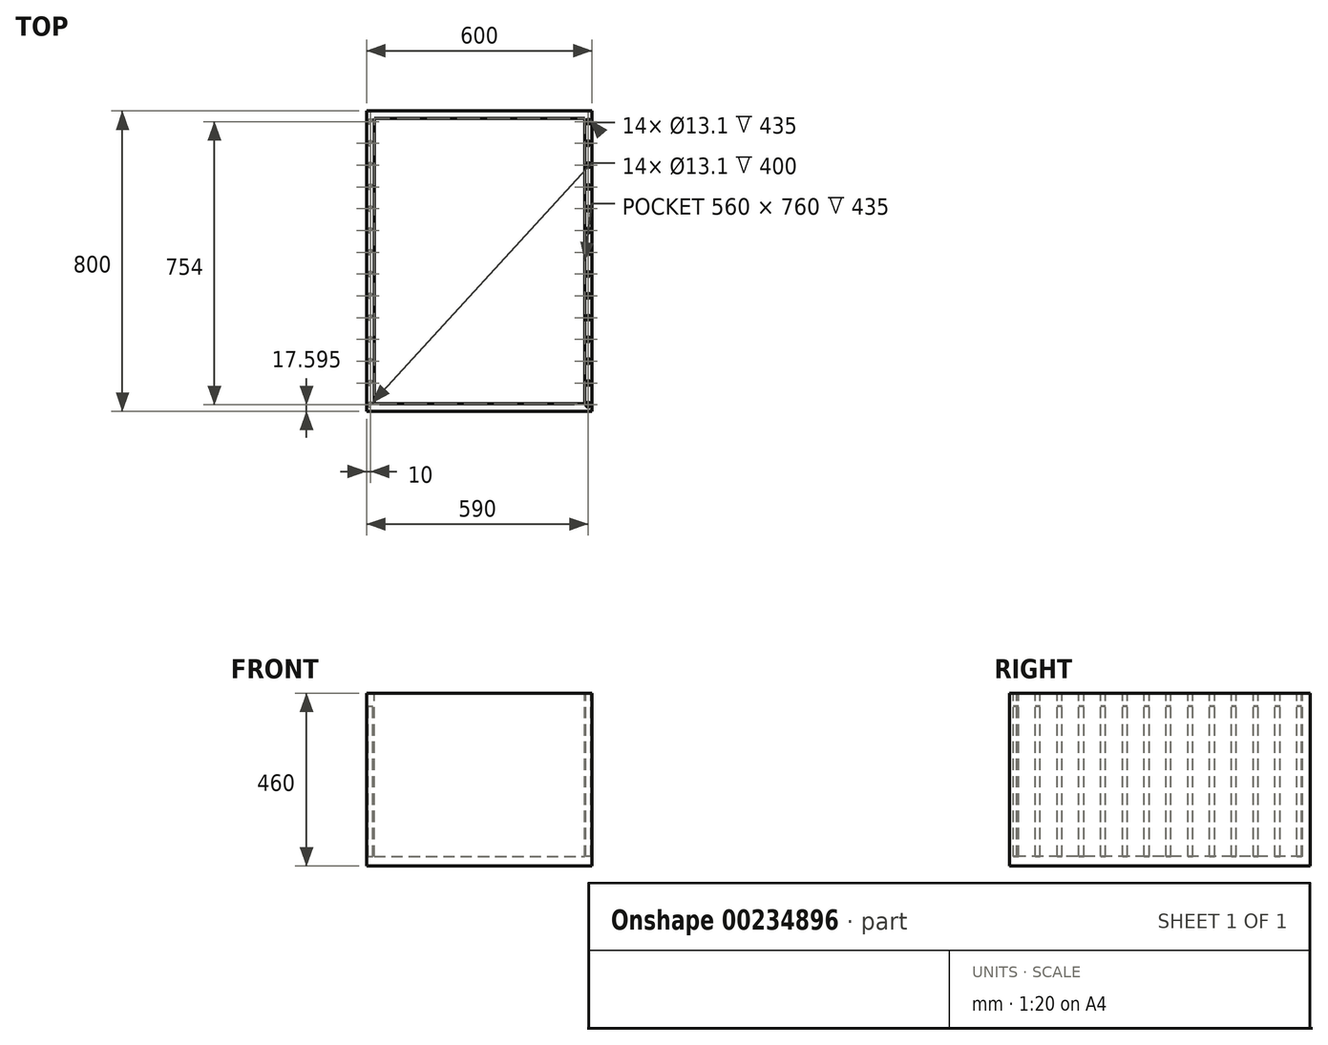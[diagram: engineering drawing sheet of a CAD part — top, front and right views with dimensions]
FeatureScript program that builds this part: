
annotation { "Feature Type Name" : "Feature", "Feature Type Description" : "" }
export const myFeature = defineFeature(function(context is Context, id is Id, definition is map)
    precondition{}
    {
        {
            var Q0;
            Q0=qCreatedBy(makeId("Top.planeOp"),FACE);
            var sketch = newSketch(context, id + "F0", { "sketchPlane" : qUnion([Q0])});
            skLineSegment(sketch, "E0.bottom", {"start": v(-307, 349) * mm, "end": v(293, 349) * mm});
            skLineSegment(sketch, "E0.top", {"start": v(-307, -451) * mm, "end": v(293, -451) * mm});
            skLineSegment(sketch, "E0.left", {"start": v(-307, 349) * mm, "end": v(-307, -451) * mm});
            skLineSegment(sketch, "E0.right", {"start": v(293, 349) * mm, "end": v(293, -451) * mm});
            skLineSegment(sketch, "E1.0", {"start": v(-287, 329) * mm, "end": v(273, 329) * mm});
            skLineSegment(sketch, "E1.1", {"start": v(-287, 329) * mm, "end": v(-287, -431) * mm});
            skLineSegment(sketch, "E1.2", {"start": v(-287, -431) * mm, "end": v(273, -431) * mm});
            skLineSegment(sketch, "E1.3", {"start": v(273, 329) * mm, "end": v(273, -431) * mm});
            skLineSegment(sketch, "E2", {"start": v(-307, -51) * mm, "end": v(-287, -51) * mm, "construction": true});
            skLineSegment(sketch, "E3", {"start": v(-287, -51) * mm, "end": v(-297, -51) * mm, "construction": true});
            skLineSegment(sketch, "E4", {"start": v(-297, -51) * mm, "end": v(-297, -27.4) * mm, "construction": true});
            skCircle(sketch, "E5", {"center": v(-297, -27.4) * mm, "radius": 6.55 * mm});
            skCircle(sketch, "E6.0.1.0", {"center": v(-297, 30.6) * mm, "radius": 6.55 * mm});
            skCircle(sketch, "E6.0.2.0", {"center": v(-297, 88.6) * mm, "radius": 6.55 * mm});
            skCircle(sketch, "E6.0.3.0", {"center": v(-297, 146.6) * mm, "radius": 6.55 * mm});
            skCircle(sketch, "E6.0.4.0", {"center": v(-297, 204.6) * mm, "radius": 6.55 * mm});
            skCircle(sketch, "E6.0.5.0", {"center": v(-297, 262.6) * mm, "radius": 6.55 * mm});
            skCircle(sketch, "E6.0.6.0", {"center": v(-297, 320.6) * mm, "radius": 6.55 * mm});
            skLineSegment(sketch, "E6.direction1", {"start": v(-297, -27.4) * mm, "end": v(-272, -27.4) * mm, "construction": true});
            skLineSegment(sketch, "E6.direction2", {"start": v(-297, -27.4) * mm, "end": v(-297, 30.6) * mm, "construction": true});
            skCircle(sketch, "E7.0.1.0", {"center": v(-297, -85.4) * mm, "radius": 6.55 * mm});
            skCircle(sketch, "E7.0.2.0", {"center": v(-297, -143.4) * mm, "radius": 6.55 * mm});
            skCircle(sketch, "E7.0.3.0", {"center": v(-297, -201.4) * mm, "radius": 6.55 * mm});
            skCircle(sketch, "E7.0.4.0", {"center": v(-297, -259.4) * mm, "radius": 6.55 * mm});
            skCircle(sketch, "E7.0.5.0", {"center": v(-297, -317.4) * mm, "radius": 6.55 * mm});
            skCircle(sketch, "E7.0.6.0", {"center": v(-297, -375.4) * mm, "radius": 6.55 * mm});
            skCircle(sketch, "E7.0.7.0", {"center": v(-297, -433.4) * mm, "radius": 6.55 * mm});
            skLineSegment(sketch, "E7.direction1", {"start": v(-297, -27.4) * mm, "end": v(-257, -27.4) * mm, "construction": true});
            skLineSegment(sketch, "E7.direction2", {"start": v(-297, -27.4) * mm, "end": v(-297, -85.4) * mm, "construction": true});
            skLineSegment(sketch, "E8", {"start": v(-7, 329) * mm, "end": v(-7, -431) * mm, "construction": true});
            skCircle(sketch, "E9.MirrorC", {"center": v(283, 320.6) * mm, "radius": 6.55 * mm});
            skCircle(sketch, "E10.MirrorC", {"center": v(283, 262.6) * mm, "radius": 6.55 * mm});
            skCircle(sketch, "E11.MirrorC", {"center": v(283, 204.6) * mm, "radius": 6.55 * mm});
            skCircle(sketch, "E12.MirrorC", {"center": v(283, 146.6) * mm, "radius": 6.55 * mm});
            skCircle(sketch, "E13.MirrorC", {"center": v(283, 88.6) * mm, "radius": 6.55 * mm});
            skCircle(sketch, "E14.MirrorC", {"center": v(283, 30.6) * mm, "radius": 6.55 * mm});
            skCircle(sketch, "E15.MirrorC", {"center": v(283, -27.4) * mm, "radius": 6.55 * mm});
            skCircle(sketch, "E16.MirrorC", {"center": v(283, -85.4) * mm, "radius": 6.55 * mm});
            skCircle(sketch, "E17.MirrorC", {"center": v(283, -143.4) * mm, "radius": 6.55 * mm});
            skCircle(sketch, "E18.MirrorC", {"center": v(283, -201.4) * mm, "radius": 6.55 * mm});
            skCircle(sketch, "E19.MirrorC", {"center": v(283, -259.4) * mm, "radius": 6.55 * mm});
            skCircle(sketch, "E20.MirrorC", {"center": v(283, -317.4) * mm, "radius": 6.55 * mm});
            skCircle(sketch, "E21.MirrorC", {"center": v(283, -375.4) * mm, "radius": 6.55 * mm});
            skCircle(sketch, "E22.MirrorC", {"center": v(283, -433.4) * mm, "radius": 6.55 * mm});
            skSolve(sketch);
        }
        {
            var Q0;
            Q0=makeQuery(id+"F0.imprint","IMPRINT",FACE,{"disambiguationData":[TD([[makeQuery(id+"F0.imprint","IMPRINT",EDGE,{"derivedFrom":sQuery(id+"F0.wireOp",EDGE,"E0.bottom")}),-1.0]])]});
            var Q1;
            Q1=makeQuery(id+"F0.imprint","IMPRINT",FACE,{"disambiguationData":[TD([[makeQuery(id+"F0.imprint","IMPRINT",EDGE,{"derivedFrom":sQuery(id+"F0.wireOp",EDGE,"E22.MirrorC")}),-1.0]])]});
            var Q2;
            Q2=makeQuery(id+"F0.imprint","IMPRINT",FACE,{"disambiguationData":[TD([[makeQuery(id+"F0.imprint","IMPRINT",EDGE,{"derivedFrom":sQuery(id+"F0.wireOp",EDGE,"E21.MirrorC")}),-1.0]])]});
            var Q3;
            Q3=makeQuery(id+"F0.imprint","IMPRINT",FACE,{"disambiguationData":[TD([[makeQuery(id+"F0.imprint","IMPRINT",EDGE,{"derivedFrom":sQuery(id+"F0.wireOp",EDGE,"E20.MirrorC")}),-1.0]])]});
            var Q4;
            Q4=makeQuery(id+"F0.imprint","IMPRINT",FACE,{"disambiguationData":[TD([[makeQuery(id+"F0.imprint","IMPRINT",EDGE,{"derivedFrom":sQuery(id+"F0.wireOp",EDGE,"E19.MirrorC")}),-1.0]])]});
            var Q5;
            Q5=makeQuery(id+"F0.imprint","IMPRINT",FACE,{"disambiguationData":[TD([[makeQuery(id+"F0.imprint","IMPRINT",EDGE,{"derivedFrom":sQuery(id+"F0.wireOp",EDGE,"E18.MirrorC")}),-1.0]])]});
            var Q6;
            Q6=makeQuery(id+"F0.imprint","IMPRINT",FACE,{"disambiguationData":[TD([[makeQuery(id+"F0.imprint","IMPRINT",EDGE,{"derivedFrom":sQuery(id+"F0.wireOp",EDGE,"E17.MirrorC")}),-1.0]])]});
            var Q7;
            Q7=makeQuery(id+"F0.imprint","IMPRINT",FACE,{"disambiguationData":[TD([[makeQuery(id+"F0.imprint","IMPRINT",EDGE,{"derivedFrom":sQuery(id+"F0.wireOp",EDGE,"E16.MirrorC")}),-1.0]])]});
            var Q8;
            Q8=makeQuery(id+"F0.imprint","IMPRINT",FACE,{"disambiguationData":[TD([[makeQuery(id+"F0.imprint","IMPRINT",EDGE,{"derivedFrom":sQuery(id+"F0.wireOp",EDGE,"E15.MirrorC")}),-1.0]])]});
            var Q9;
            Q9=makeQuery(id+"F0.imprint","IMPRINT",FACE,{"disambiguationData":[TD([[makeQuery(id+"F0.imprint","IMPRINT",EDGE,{"derivedFrom":sQuery(id+"F0.wireOp",EDGE,"E14.MirrorC")}),-1.0]])]});
            var Q10;
            Q10=makeQuery(id+"F0.imprint","IMPRINT",FACE,{"disambiguationData":[TD([[makeQuery(id+"F0.imprint","IMPRINT",EDGE,{"derivedFrom":sQuery(id+"F0.wireOp",EDGE,"E13.MirrorC")}),-1.0]])]});
            var Q11;
            Q11=makeQuery(id+"F0.imprint","IMPRINT",FACE,{"disambiguationData":[TD([[makeQuery(id+"F0.imprint","IMPRINT",EDGE,{"derivedFrom":sQuery(id+"F0.wireOp",EDGE,"E12.MirrorC")}),-1.0]])]});
            var Q12;
            Q12=makeQuery(id+"F0.imprint","IMPRINT",FACE,{"disambiguationData":[TD([[makeQuery(id+"F0.imprint","IMPRINT",EDGE,{"derivedFrom":sQuery(id+"F0.wireOp",EDGE,"E11.MirrorC")}),-1.0]])]});
            var Q13;
            Q13=makeQuery(id+"F0.imprint","IMPRINT",FACE,{"disambiguationData":[TD([[makeQuery(id+"F0.imprint","IMPRINT",EDGE,{"derivedFrom":sQuery(id+"F0.wireOp",EDGE,"E10.MirrorC")}),-1.0]])]});
            var Q14;
            Q14=makeQuery(id+"F0.imprint","IMPRINT",FACE,{"disambiguationData":[TD([[makeQuery(id+"F0.imprint","IMPRINT",EDGE,{"derivedFrom":sQuery(id+"F0.wireOp",EDGE,"E9.MirrorC")}),-1.0]])]});
            var Q15;
            Q15=makeQuery(id+"F0.imprint","IMPRINT",FACE,{"disambiguationData":[TD([[makeQuery(id+"F0.imprint","IMPRINT",EDGE,{"derivedFrom":sQuery(id+"F0.wireOp",EDGE,"E6.0.6.0")}),1.0]])]});
            var Q16;
            Q16=makeQuery(id+"F0.imprint","IMPRINT",FACE,{"disambiguationData":[TD([[makeQuery(id+"F0.imprint","IMPRINT",EDGE,{"derivedFrom":sQuery(id+"F0.wireOp",EDGE,"E6.0.5.0")}),1.0]])]});
            var Q17;
            Q17=makeQuery(id+"F0.imprint","IMPRINT",FACE,{"disambiguationData":[TD([[makeQuery(id+"F0.imprint","IMPRINT",EDGE,{"derivedFrom":sQuery(id+"F0.wireOp",EDGE,"E6.0.4.0")}),1.0]])]});
            var Q18;
            Q18=makeQuery(id+"F0.imprint","IMPRINT",FACE,{"disambiguationData":[TD([[makeQuery(id+"F0.imprint","IMPRINT",EDGE,{"derivedFrom":sQuery(id+"F0.wireOp",EDGE,"E6.0.3.0")}),1.0]])]});
            var Q19;
            Q19=makeQuery(id+"F0.imprint","IMPRINT",FACE,{"disambiguationData":[TD([[makeQuery(id+"F0.imprint","IMPRINT",EDGE,{"derivedFrom":sQuery(id+"F0.wireOp",EDGE,"E6.0.2.0")}),1.0]])]});
            var Q20;
            Q20=makeQuery(id+"F0.imprint","IMPRINT",FACE,{"disambiguationData":[TD([[makeQuery(id+"F0.imprint","IMPRINT",EDGE,{"derivedFrom":sQuery(id+"F0.wireOp",EDGE,"E6.0.1.0")}),1.0]])]});
            var Q21;
            Q21=makeQuery(id+"F0.imprint","IMPRINT",FACE,{"disambiguationData":[TD([[makeQuery(id+"F0.imprint","IMPRINT",EDGE,{"derivedFrom":sQuery(id+"F0.wireOp",EDGE,"E5")}),1.0]])]});
            var Q22;
            Q22=makeQuery(id+"F0.imprint","IMPRINT",FACE,{"disambiguationData":[TD([[makeQuery(id+"F0.imprint","IMPRINT",EDGE,{"derivedFrom":sQuery(id+"F0.wireOp",EDGE,"E7.0.1.0")}),1.0]])]});
            var Q23;
            Q23=makeQuery(id+"F0.imprint","IMPRINT",FACE,{"disambiguationData":[TD([[makeQuery(id+"F0.imprint","IMPRINT",EDGE,{"derivedFrom":sQuery(id+"F0.wireOp",EDGE,"E7.0.2.0")}),1.0]])]});
            var Q24;
            Q24=makeQuery(id+"F0.imprint","IMPRINT",FACE,{"disambiguationData":[TD([[makeQuery(id+"F0.imprint","IMPRINT",EDGE,{"derivedFrom":sQuery(id+"F0.wireOp",EDGE,"E7.0.3.0")}),1.0]])]});
            var Q25;
            Q25=makeQuery(id+"F0.imprint","IMPRINT",FACE,{"disambiguationData":[TD([[makeQuery(id+"F0.imprint","IMPRINT",EDGE,{"derivedFrom":sQuery(id+"F0.wireOp",EDGE,"E7.0.4.0")}),1.0]])]});
            var Q26;
            Q26=makeQuery(id+"F0.imprint","IMPRINT",FACE,{"disambiguationData":[TD([[makeQuery(id+"F0.imprint","IMPRINT",EDGE,{"derivedFrom":sQuery(id+"F0.wireOp",EDGE,"E7.0.5.0")}),1.0]])]});
            var Q27;
            Q27=makeQuery(id+"F0.imprint","IMPRINT",FACE,{"disambiguationData":[TD([[makeQuery(id+"F0.imprint","IMPRINT",EDGE,{"derivedFrom":sQuery(id+"F0.wireOp",EDGE,"E7.0.6.0")}),1.0]])]});
            var Q28;
            Q28=makeQuery(id+"F0.imprint","IMPRINT",FACE,{"disambiguationData":[TD([[makeQuery(id+"F0.imprint","IMPRINT",EDGE,{"derivedFrom":sQuery(id+"F0.wireOp",EDGE,"E7.0.7.0")}),1.0]])]});
            extrude(context, id + "F1", {"entities" : qUnion([Q0, Q1, Q2, Q3, Q4, Q5, Q6, Q7, Q8, Q9, Q10, Q11, Q12, Q13, Q14, Q15, Q16, Q17, Q18, Q19, Q20, Q21, Q22, Q23, Q24, Q25, Q26, Q27, Q28]), "oppositeDirection" : true, "depth" : 35 * mm});
        }
        {
            var Q0;
            Q0=makeQuery(id+"F1.opExtrude","CAP_FACE",FACE,{"disambiguationData":[OSD([sQuery(id+"F0.wireOp",EDGE,"E0.bottom"),sQuery(id+"F0.wireOp",EDGE,"E0.top"),sQuery(id+"F0.wireOp",EDGE,"E0.left"),sQuery(id+"F0.wireOp",EDGE,"E0.right"),sQuery(id+"F0.wireOp",EDGE,"E1.0"),sQuery(id+"F0.wireOp",EDGE,"E1.1"),sQuery(id+"F0.wireOp",EDGE,"E1.2"),sQuery(id+"F0.wireOp",EDGE,"E1.3")])],"isStart":false});
            var sketch = newSketch(context, id + "F2", { "sketchPlane" : qUnion([Q0])});
            skCircle(sketch, "E23.0", {"center": v(283, 85.4) * mm, "radius": 6.55 * mm});
            skCircle(sketch, "E23.1", {"center": v(283, -320.6) * mm, "radius": 6.55 * mm});
            skCircle(sketch, "E23.2", {"center": v(283, -204.6) * mm, "radius": 6.55 * mm});
            skCircle(sketch, "E23.3", {"center": v(283, -262.6) * mm, "radius": 6.55 * mm});
            skCircle(sketch, "E23.4", {"center": v(283, 143.4) * mm, "radius": 6.55 * mm});
            skCircle(sketch, "E23.5", {"center": v(283, 259.4) * mm, "radius": 6.55 * mm});
            skCircle(sketch, "E23.6", {"center": v(283, -146.6) * mm, "radius": 6.55 * mm});
            skCircle(sketch, "E23.7", {"center": v(283, 317.4) * mm, "radius": 6.55 * mm});
            skCircle(sketch, "E23.8", {"center": v(283, 201.4) * mm, "radius": 6.55 * mm});
            skCircle(sketch, "E23.9", {"center": v(283, -30.6) * mm, "radius": 6.55 * mm});
            skCircle(sketch, "E23.10", {"center": v(283, 27.4) * mm, "radius": 6.55 * mm});
            skCircle(sketch, "E23.11", {"center": v(283, 433.4) * mm, "radius": 6.55 * mm});
            skCircle(sketch, "E23.12", {"center": v(283, 375.4) * mm, "radius": 6.55 * mm});
            skCircle(sketch, "E23.13", {"center": v(283, -88.6) * mm, "radius": 6.55 * mm});
            skCircle(sketch, "E24.0", {"center": v(-297, -30.6) * mm, "radius": 6.55 * mm});
            skCircle(sketch, "E24.1", {"center": v(-297, 259.4) * mm, "radius": 6.55 * mm});
            skCircle(sketch, "E24.2", {"center": v(-297, -320.6) * mm, "radius": 6.55 * mm});
            skLineSegment(sketch, "E24.3", {"start": v(-297, 51) * mm, "end": v(-297, 27.4) * mm});
            skCircle(sketch, "E24.4", {"center": v(-297, -204.6) * mm, "radius": 6.55 * mm});
            skCircle(sketch, "E24.5", {"center": v(-297, -146.6) * mm, "radius": 6.55 * mm});
            skCircle(sketch, "E24.6", {"center": v(-297, 201.4) * mm, "radius": 6.55 * mm});
            skCircle(sketch, "E24.7", {"center": v(-297, 317.4) * mm, "radius": 6.55 * mm});
            skCircle(sketch, "E24.8", {"center": v(-297, 375.4) * mm, "radius": 6.55 * mm});
            skCircle(sketch, "E24.9", {"center": v(-297, -88.6) * mm, "radius": 6.55 * mm});
            skCircle(sketch, "E24.10", {"center": v(-297, 143.4) * mm, "radius": 6.55 * mm});
            skCircle(sketch, "E24.11", {"center": v(-297, 27.4) * mm, "radius": 6.55 * mm});
            skLineSegment(sketch, "E24.12", {"start": v(-297, 27.4) * mm, "end": v(-297, 85.4) * mm});
            skCircle(sketch, "E24.13", {"center": v(-297, -262.6) * mm, "radius": 6.55 * mm});
            skCircle(sketch, "E24.14", {"center": v(-297, 85.4) * mm, "radius": 6.55 * mm});
            skLineSegment(sketch, "E24.15", {"start": v(-297, 27.4) * mm, "end": v(-297, -30.6) * mm});
            skCircle(sketch, "E24.16", {"center": v(-297, 433.4) * mm, "radius": 6.55 * mm});
            skSolve(sketch);
        }
        {
            var Q0;
            Q0=makeQuery(id+"F2.imprint","IMPRINT",FACE,{"disambiguationData":[TD([[makeQuery(id+"F2.imprint","IMPRINT",EDGE,{"derivedFrom":sQuery(id+"F2.wireOp",EDGE,"E24.16")}),-1.0]])]});
            var Q1;
            Q1=makeQuery(id+"F2.imprint","IMPRINT",FACE,{"disambiguationData":[TD([[makeQuery(id+"F2.imprint","IMPRINT",EDGE,{"derivedFrom":sQuery(id+"F2.wireOp",EDGE,"E24.10")}),-1.0]])]});
            var Q2;
            Q2=makeQuery(id+"F2.imprint","IMPRINT",FACE,{"disambiguationData":[TD([[makeQuery(id+"F2.imprint","IMPRINT",EDGE,{"derivedFrom":sQuery(id+"F2.wireOp",EDGE,"E24.8")}),-1.0]])]});
            var Q3;
            Q3=makeQuery(id+"F2.imprint","IMPRINT",FACE,{"disambiguationData":[TD([[makeQuery(id+"F2.imprint","IMPRINT",EDGE,{"derivedFrom":sQuery(id+"F2.wireOp",EDGE,"E24.4")}),-1.0]])]});
            var Q4;
            {var subQ0=sQuery(id+"F2.wireOp",EDGE,"E24.12");var subQ1=sQuery(id+"F2.wireOp",EDGE,"E24.11");var subQ2=makeQuery(id+"F2.imprint","INTERSECT",VERTEX,{"derivedFrom":[subQ1,subQ0]});Q4=makeQuery(id+"F2.imprint","IMPRINT",FACE,{"disambiguationData":[TD([[makeQuery(id+"F2.imprint","IMPRINT",EDGE,{"disambiguationData":[TD([[subQ2,-1.0]])],"derivedFrom":subQ1}),-1.0]])]});}
            var Q5;
            Q5=makeQuery(id+"F2.imprint","IMPRINT",FACE,{"disambiguationData":[TD([[makeQuery(id+"F2.imprint","IMPRINT",EDGE,{"derivedFrom":sQuery(id+"F2.wireOp",EDGE,"E24.13")}),-1.0]])]});
            var Q6;
            Q6=makeQuery(id+"F2.imprint","IMPRINT",FACE,{"disambiguationData":[TD([[makeQuery(id+"F2.imprint","IMPRINT",EDGE,{"derivedFrom":sQuery(id+"F2.wireOp",EDGE,"E24.5")}),-1.0]])]});
            var Q7;
            Q7=makeQuery(id+"F2.imprint","IMPRINT",FACE,{"disambiguationData":[TD([[makeQuery(id+"F2.imprint","IMPRINT",EDGE,{"derivedFrom":sQuery(id+"F2.wireOp",EDGE,"E24.1")}),-1.0]])]});
            var Q8;
            Q8=makeQuery(id+"F2.imprint","IMPRINT",FACE,{"disambiguationData":[TD([[makeQuery(id+"F2.imprint","IMPRINT",EDGE,{"derivedFrom":sQuery(id+"F2.wireOp",EDGE,"E23.13")}),1.0]])]});
            var Q9;
            Q9=makeQuery(id+"F2.imprint","IMPRINT",FACE,{"disambiguationData":[TD([[makeQuery(id+"F2.imprint","IMPRINT",EDGE,{"derivedFrom":sQuery(id+"F2.wireOp",EDGE,"E24.0")}),-1.0]])]});
            var Q10;
            Q10=makeQuery(id+"F2.imprint","IMPRINT",FACE,{"disambiguationData":[TD([[makeQuery(id+"F2.imprint","IMPRINT",EDGE,{"derivedFrom":sQuery(id+"F2.wireOp",EDGE,"E23.0")}),1.0]])]});
            var Q11;
            Q11=makeQuery(id+"F2.imprint","IMPRINT",FACE,{"disambiguationData":[TD([[makeQuery(id+"F2.imprint","IMPRINT",EDGE,{"derivedFrom":sQuery(id+"F2.wireOp",EDGE,"E23.1")}),1.0]])]});
            var Q12;
            Q12=makeQuery(id+"F2.imprint","IMPRINT",FACE,{"disambiguationData":[TD([[makeQuery(id+"F2.imprint","IMPRINT",EDGE,{"derivedFrom":sQuery(id+"F2.wireOp",EDGE,"E23.2")}),1.0]])]});
            var Q13;
            Q13=makeQuery(id+"F2.imprint","IMPRINT",FACE,{"disambiguationData":[TD([[makeQuery(id+"F2.imprint","IMPRINT",EDGE,{"derivedFrom":sQuery(id+"F2.wireOp",EDGE,"E23.3")}),1.0]])]});
            var Q14;
            Q14=makeQuery(id+"F2.imprint","IMPRINT",FACE,{"disambiguationData":[TD([[makeQuery(id+"F2.imprint","IMPRINT",EDGE,{"derivedFrom":sQuery(id+"F2.wireOp",EDGE,"E23.4")}),1.0]])]});
            var Q15;
            Q15=makeQuery(id+"F2.imprint","IMPRINT",FACE,{"disambiguationData":[TD([[makeQuery(id+"F2.imprint","IMPRINT",EDGE,{"derivedFrom":sQuery(id+"F2.wireOp",EDGE,"E23.5")}),1.0]])]});
            var Q16;
            Q16=makeQuery(id+"F2.imprint","IMPRINT",FACE,{"disambiguationData":[TD([[makeQuery(id+"F2.imprint","IMPRINT",EDGE,{"derivedFrom":sQuery(id+"F2.wireOp",EDGE,"E23.6")}),1.0]])]});
            var Q17;
            Q17=makeQuery(id+"F2.imprint","IMPRINT",FACE,{"disambiguationData":[TD([[makeQuery(id+"F2.imprint","IMPRINT",EDGE,{"derivedFrom":sQuery(id+"F2.wireOp",EDGE,"E23.7")}),1.0]])]});
            var Q18;
            Q18=makeQuery(id+"F2.imprint","IMPRINT",FACE,{"disambiguationData":[TD([[makeQuery(id+"F2.imprint","IMPRINT",EDGE,{"derivedFrom":sQuery(id+"F2.wireOp",EDGE,"E23.8")}),1.0]])]});
            var Q19;
            Q19=makeQuery(id+"F2.imprint","IMPRINT",FACE,{"disambiguationData":[TD([[makeQuery(id+"F2.imprint","IMPRINT",EDGE,{"derivedFrom":sQuery(id+"F2.wireOp",EDGE,"E23.9")}),1.0]])]});
            var Q20;
            Q20=makeQuery(id+"F2.imprint","IMPRINT",FACE,{"disambiguationData":[TD([[makeQuery(id+"F2.imprint","IMPRINT",EDGE,{"derivedFrom":sQuery(id+"F2.wireOp",EDGE,"E23.10")}),1.0]])]});
            var Q21;
            Q21=makeQuery(id+"F2.imprint","IMPRINT",FACE,{"disambiguationData":[TD([[makeQuery(id+"F2.imprint","IMPRINT",EDGE,{"derivedFrom":sQuery(id+"F2.wireOp",EDGE,"E24.14")}),-1.0]])]});
            var Q22;
            Q22=makeQuery(id+"F2.imprint","IMPRINT",FACE,{"disambiguationData":[TD([[makeQuery(id+"F2.imprint","IMPRINT",EDGE,{"derivedFrom":sQuery(id+"F2.wireOp",EDGE,"E24.6")}),-1.0]])]});
            var Q23;
            Q23=makeQuery(id+"F2.imprint","IMPRINT",FACE,{"disambiguationData":[TD([[makeQuery(id+"F2.imprint","IMPRINT",EDGE,{"derivedFrom":sQuery(id+"F2.wireOp",EDGE,"E24.9")}),-1.0]])]});
            var Q24;
            Q24=makeQuery(id+"F2.imprint","IMPRINT",FACE,{"disambiguationData":[TD([[makeQuery(id+"F2.imprint","IMPRINT",EDGE,{"derivedFrom":sQuery(id+"F2.wireOp",EDGE,"E24.7")}),-1.0]])]});
            var Q25;
            Q25=makeQuery(id+"F2.imprint","IMPRINT",FACE,{"disambiguationData":[TD([[makeQuery(id+"F2.imprint","IMPRINT",EDGE,{"derivedFrom":sQuery(id+"F2.wireOp",EDGE,"E24.2")}),-1.0]])]});
            var Q26;
            {var subQ0=sQuery(id+"F2.wireOp",EDGE,"E24.12");var subQ1=sQuery(id+"F2.wireOp",EDGE,"E24.11");var subQ2=makeQuery(id+"F2.imprint","INTERSECT",VERTEX,{"derivedFrom":[subQ1,subQ0]});Q26=makeQuery(id+"F2.imprint","IMPRINT",FACE,{"disambiguationData":[TD([[makeQuery(id+"F2.imprint","IMPRINT",EDGE,{"disambiguationData":[TD([[subQ2,1.0]])],"derivedFrom":subQ1}),-1.0]])]});}
            var Q27;
            Q27=makeQuery(id+"F2.imprint","IMPRINT",FACE,{"disambiguationData":[TD([[makeQuery(id+"F2.imprint","IMPRINT",EDGE,{"derivedFrom":sQuery(id+"F2.wireOp",EDGE,"E23.11")}),1.0]])]});
            var Q28;
            Q28=makeQuery(id+"F2.imprint","IMPRINT",FACE,{"disambiguationData":[TD([[makeQuery(id+"F2.imprint","IMPRINT",EDGE,{"derivedFrom":sQuery(id+"F2.wireOp",EDGE,"E23.12")}),1.0]])]});
            var Q29;
            Q29=sQuery(id+"F2.wireOp",EDGE,"E24.15");
            var Q30;
            Q30=sQuery(id+"F2.wireOp",EDGE,"E24.14");
            var Q31;
            Q31=sQuery(id+"F2.wireOp",EDGE,"E23.13");
            var Q32;
            Q32=sQuery(id+"F2.wireOp",EDGE,"E23.8");
            var Q33;
            Q33=sQuery(id+"F2.wireOp",EDGE,"E24.8");
            var Q34;
            Q34=sQuery(id+"F2.wireOp",EDGE,"E24.4");
            var Q35;
            Q35=sQuery(id+"F2.wireOp",EDGE,"E24.12");
            var Q36;
            Q36=sQuery(id+"F2.wireOp",EDGE,"E24.13");
            var Q37;
            Q37=sQuery(id+"F2.wireOp",EDGE,"E24.9");
            var Q38;
            Q38=sQuery(id+"F2.wireOp",EDGE,"E24.6");
            var Q39;
            Q39=sQuery(id+"F2.wireOp",EDGE,"E24.2");
            var Q40;
            Q40=sQuery(id+"F2.wireOp",EDGE,"E24.10");
            var Q41;
            Q41=sQuery(id+"F2.wireOp",EDGE,"E24.16");
            var Q42;
            Q42=sQuery(id+"F2.wireOp",EDGE,"E24.7");
            var Q43;
            Q43=sQuery(id+"F2.wireOp",EDGE,"E24.3");
            var Q44;
            Q44=sQuery(id+"F2.wireOp",EDGE,"E24.1");
            var Q45;
            Q45=sQuery(id+"F2.wireOp",EDGE,"E23.0");
            var Q46;
            Q46=sQuery(id+"F2.wireOp",EDGE,"E23.1");
            var Q47;
            Q47=sQuery(id+"F2.wireOp",EDGE,"E23.2");
            var Q48;
            Q48=sQuery(id+"F2.wireOp",EDGE,"E23.3");
            var Q49;
            Q49=sQuery(id+"F2.wireOp",EDGE,"E23.4");
            var Q50;
            Q50=sQuery(id+"F2.wireOp",EDGE,"E23.5");
            var Q51;
            Q51=sQuery(id+"F2.wireOp",EDGE,"E23.6");
            var Q52;
            Q52=sQuery(id+"F2.wireOp",EDGE,"E23.7");
            var Q53;
            Q53=sQuery(id+"F2.wireOp",EDGE,"E23.9");
            var Q54;
            Q54=sQuery(id+"F2.wireOp",EDGE,"E23.10");
            var Q55;
            Q55=sQuery(id+"F2.wireOp",EDGE,"E23.12");
            var Q56;
            Q56=sQuery(id+"F2.wireOp",EDGE,"E24.5");
            var Q57;
            Q57=sQuery(id+"F2.wireOp",EDGE,"E24.0");
            var Q58;
            Q58=sQuery(id+"F2.wireOp",EDGE,"E24.11");
            var Q59;
            Q59=sQuery(id+"F2.wireOp",EDGE,"E23.11");
            extrude(context, id + "F3", {"entities" : qUnion([Q0, Q1, Q2, Q3, Q4, Q5, Q6, Q7, Q8, Q9, Q10, Q11, Q12, Q13, Q14, Q15, Q16, Q17, Q18, Q19, Q20, Q21, Q22, Q23, Q24, Q25, Q26, Q27, Q28]), "operationType" : NewBodyOperationType.ADD, "surfaceEntities" : qUnion([Q29, Q30, Q31, Q32, Q33, Q34, Q35, Q36, Q37, Q38, Q39, Q40, Q41, Q42, Q43, Q44, Q45, Q46, Q47, Q48, Q49, Q50, Q51, Q52, Q53, Q54, Q55, Q56, Q57, Q58, Q59]), "depth" : 400 * mm});
        }
        {
            var Q0;
            Q0=makeQuery(id+"F3.opExtrude","CAP_FACE",FACE,{"disambiguationData":[OSD([sQuery(id+"F2.wireOp",EDGE,"E24.16")])],"isStart":false});
            var sketch = newSketch(context, id + "F4", { "sketchPlane" : qUnion([Q0])});
            skLineSegment(sketch, "E25.0", {"start": v(-307, 451) * mm, "end": v(293, 451) * mm});
            skLineSegment(sketch, "E26.0", {"start": v(-307, -349) * mm, "end": v(-307, 451) * mm});
            skLineSegment(sketch, "E27.0", {"start": v(-307, -349) * mm, "end": v(293, -349) * mm});
            skLineSegment(sketch, "E28.0", {"start": v(293, -349) * mm, "end": v(293, 451) * mm});
            skSolve(sketch);
        }
        {
            var Q0;
            Q0 = qSketchRegion(id + "F4", true);
            extrude(context, id + "F5", {"entities" : qUnion([Q0]), "operationType" : NewBodyOperationType.ADD, "depth" : 25 * mm});
        }
    });
